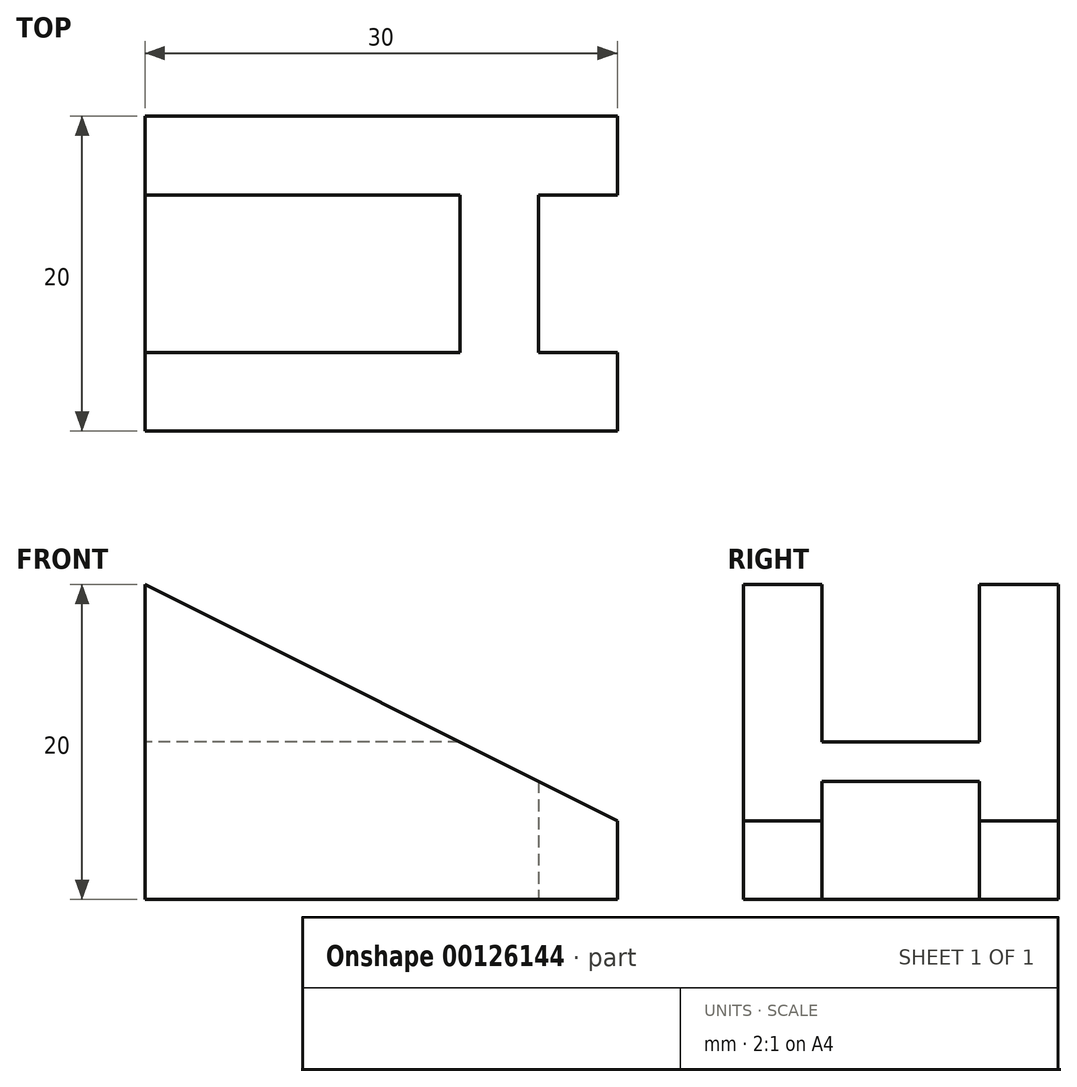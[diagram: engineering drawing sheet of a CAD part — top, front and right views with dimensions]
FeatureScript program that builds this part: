
annotation { "Feature Type Name" : "Feature", "Feature Type Description" : "" }
export const myFeature = defineFeature(function(context is Context, id is Id, definition is map)
    precondition{}
    {
        {
            var Q0;
            Q0=qCreatedBy(makeId("Front.planeOp"),FACE);
            var sketch = newSketch(context, id + "F0", { "sketchPlane" : qUnion([Q0])});
            skLineSegment(sketch, "E0", {"start": v(0, 0) * mm, "end": v(30, 0) * mm});
            skLineSegment(sketch, "E1", {"start": v(30, 0) * mm, "end": v(30, 5) * mm});
            skLineSegment(sketch, "E2", {"start": v(0, 0) * mm, "end": v(0, 20) * mm});
            skLineSegment(sketch, "E3", {"start": v(0, 20) * mm, "end": v(30, 5) * mm});
            skSolve(sketch);
        }
        {
            var Q0;
            Q0 = qSketchRegion(id + "F0", true);
            extrude(context, id + "F1", {"entities" : qUnion([Q0]), "depth" : 20 * mm});
        }
        {
            var Q0;
            Q0=makeQuery(id+"F1.opExtrude","SWEPT_FACE",FACE,{"disambiguationData":[OSD([sQuery(id+"F0.wireOp",EDGE,"E2")])]});
            var sketch = newSketch(context, id + "F2", { "sketchPlane" : qUnion([Q0])});
            skLineSegment(sketch, "E4", {"start": v(5, 20) * mm, "end": v(5, 10) * mm});
            skLineSegment(sketch, "E5", {"start": v(5, 10) * mm, "end": v(15, 10) * mm});
            skLineSegment(sketch, "E6", {"start": v(15, 10) * mm, "end": v(15, 20) * mm});
            skSolve(sketch);
        }
        {
            var Q0;
            Q0 = qSketchRegion(id + "F2", true);
            var Q1;
            {var subQ0=sQuery(id+"F2.wireOp",EDGE,"E4");Q1=makeQuery(id+"F2.imprint","IMPRINT",FACE,{"disambiguationData":[TD([[makeQuery(id+"F2.imprint","IMPRINT",EDGE,{"derivedFrom":subQ0}),1.0]])]});}
            extrude(context, id + "F3", {"entities" : qUnion([Q0, Q1]), "operationType" : NewBodyOperationType.REMOVE, "endBound" : BoundingType.THROUGH_ALL, "oppositeDirection" : true, "depth" : 25 * mm});
        }
        {
            var Q0;
            Q0=makeQuery(id+"F1.opExtrude","SWEPT_FACE",FACE,{"disambiguationData":[OSD([sQuery(id+"F0.wireOp",EDGE,"E0")])]});
            var sketch = newSketch(context, id + "F4", { "sketchPlane" : qUnion([Q0])});
            skLineSegment(sketch, "E7", {"start": v(30, 15) * mm, "end": v(25, 15) * mm});
            skLineSegment(sketch, "E8", {"start": v(25, 15) * mm, "end": v(25, 5) * mm});
            skLineSegment(sketch, "E9", {"start": v(25, 5) * mm, "end": v(30, 5) * mm});
            skSolve(sketch);
        }
        {
            var Q0;
            {var subQ0=sQuery(id+"F4.wireOp",EDGE,"E7");Q0=makeQuery(id+"F4.imprint","IMPRINT",FACE,{"disambiguationData":[TD([[makeQuery(id+"F4.imprint","IMPRINT",EDGE,{"derivedFrom":subQ0}),1.0]])]});}
            extrude(context, id + "F5", {"entities" : qUnion([Q0]), "operationType" : NewBodyOperationType.REMOVE, "endBound" : BoundingType.THROUGH_ALL, "oppositeDirection" : true, "depth" : 25 * mm});
        }
    });
